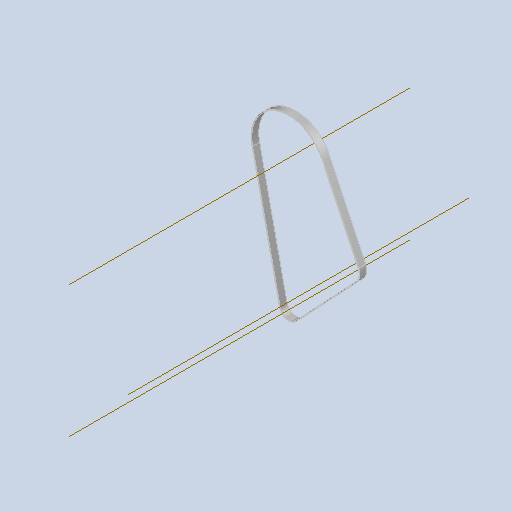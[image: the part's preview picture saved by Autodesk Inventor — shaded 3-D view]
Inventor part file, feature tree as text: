
AUTODESK INVENTOR PART (.ipt)
format: ipt  version: 2024 (Build 280153000, 153)  size: 105,984 bytes
history: native  units: mm (DEFAULTED — no unit token found)
features: other x5, plane x3, sketch x1, sweep x1
ambient origin geometry x8: Origin, YZ Plane, XZ Plane, XY Plane, X Axis, Y Axis, Z Axis, Center Point
bodies: Solid1 (feature_tree)
feature tree (10):
  sketch  "Sketch Path"  dims[d0=6.0mm d2=0.0mm d4=0.3mm d5=0.3mm d6=0.0mm d7=0.0mm d8=0.0mm d9=0.0mm d10=0.0mm d11=0.0mm d12=0.0mm d13=0.0mm]
  other  "Cross Section Plane"
  other  "Work Axis1"
  other  "Work Axis2"
  other  "Work Axis3"
  plane  "Work Plane2"
  plane  "Work Plane3"
  plane  "Work Plane4"
  sweep  "Belt"
  other  "Cross Section"
